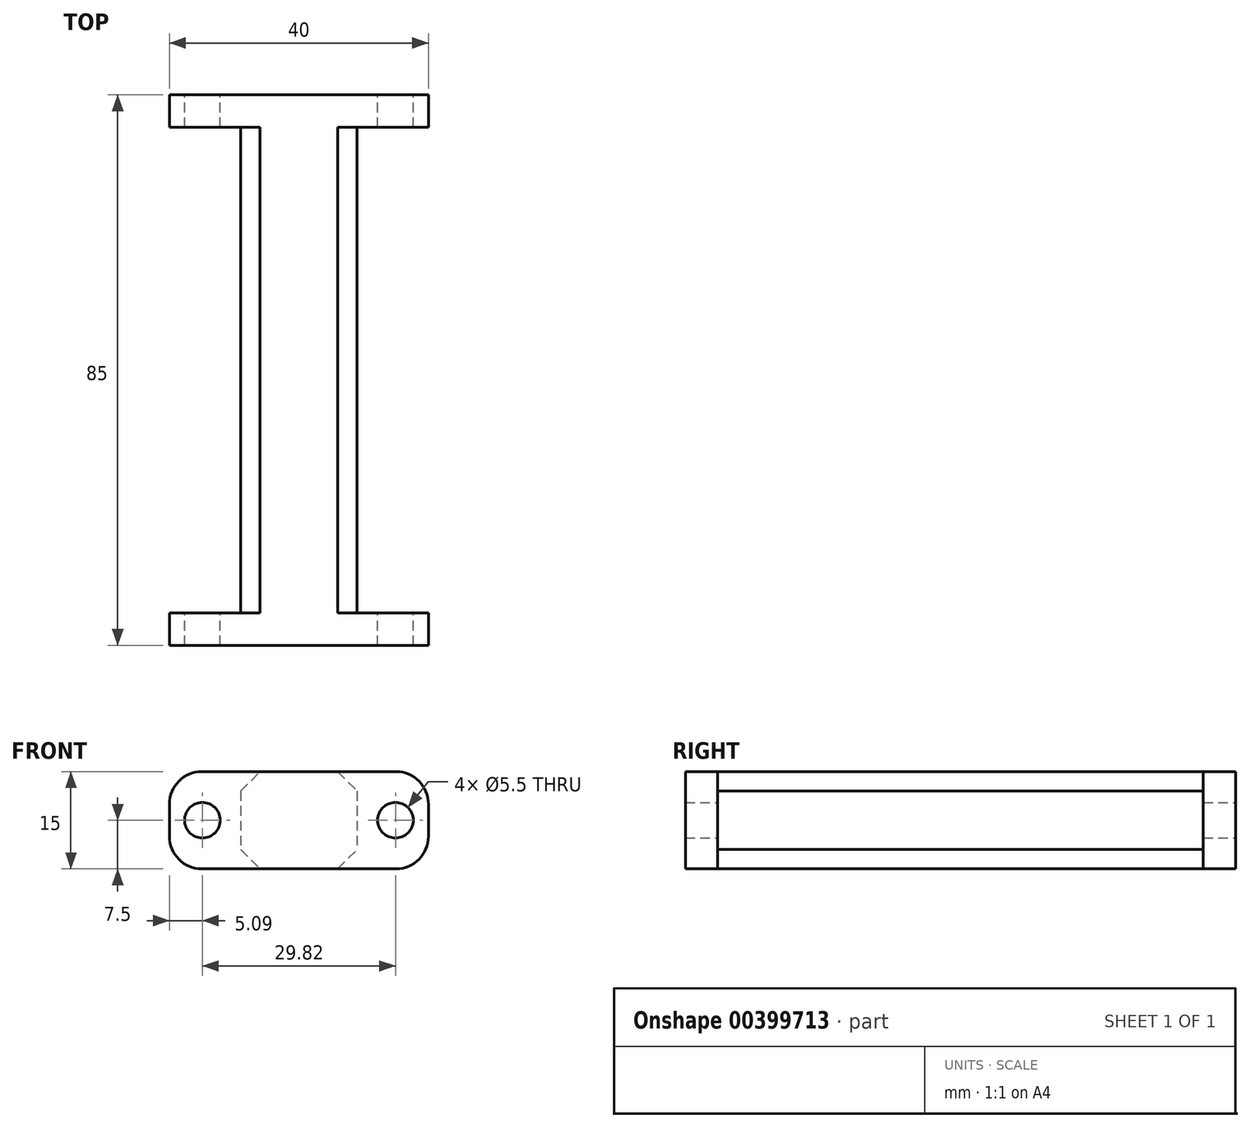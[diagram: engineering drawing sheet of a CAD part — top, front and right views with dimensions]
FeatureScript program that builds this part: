
annotation { "Feature Type Name" : "Feature", "Feature Type Description" : "" }
export const myFeature = defineFeature(function(context is Context, id is Id, definition is map)
    precondition{}
    {
        {
            var Q0;
            Q0=qCreatedBy(makeId("Top.planeOp"),FACE);
            var sketch = newSketch(context, id + "F0", { "sketchPlane" : qUnion([Q0])});
            skLineSegment(sketch, "E0.bottom", {"start": v(9, 37.5) * mm, "end": v(-9, 37.5) * mm});
            skLineSegment(sketch, "E0.top", {"start": v(9, -37.5) * mm, "end": v(-9, -37.5) * mm});
            skLineSegment(sketch, "E0.left", {"start": v(9, 37.5) * mm, "end": v(9, -37.5) * mm});
            skLineSegment(sketch, "E0.right", {"start": v(-9, 37.5) * mm, "end": v(-9, -37.5) * mm});
            skPoint(sketch, "E0.middle", {"position": v(0, 0) * mm});
            skLineSegment(sketch, "E1", {"start": v(0, -37.5) * mm, "end": v(0, -40) * mm});
            skPoint(sketch, "E1.endSnap0", {"position": v(0, -37.5) * mm});
            skLineSegment(sketch, "E2.bottom", {"start": v(20, -37.5) * mm, "end": v(-20, -37.5) * mm});
            skLineSegment(sketch, "E2.top", {"start": v(20, -42.5) * mm, "end": v(-20, -42.5) * mm});
            skLineSegment(sketch, "E2.left", {"start": v(20, -37.5) * mm, "end": v(20, -42.5) * mm});
            skLineSegment(sketch, "E2.right", {"start": v(-20, -37.5) * mm, "end": v(-20, -42.5) * mm});
            skPoint(sketch, "E2.middle", {"position": v(0, -40) * mm});
            skLineSegment(sketch, "E3", {"start": v(0, 37.5) * mm, "end": v(0, 40) * mm});
            skPoint(sketch, "E3.endSnap0", {"position": v(0, 37.5) * mm});
            skLineSegment(sketch, "E4.bottom", {"start": v(20, 42.5) * mm, "end": v(-20, 42.5) * mm});
            skLineSegment(sketch, "E4.top", {"start": v(20, 37.5) * mm, "end": v(-20, 37.5) * mm});
            skLineSegment(sketch, "E4.left", {"start": v(20, 42.5) * mm, "end": v(20, 37.5) * mm});
            skLineSegment(sketch, "E4.right", {"start": v(-20, 42.5) * mm, "end": v(-20, 37.5) * mm});
            skPoint(sketch, "E4.middle", {"position": v(0, 40) * mm});
            skSolve(sketch);
        }
        {
            var Q0;
            Q0=makeQuery(id+"F0.imprint","IMPRINT",FACE,{"disambiguationData":[TD([[makeQuery(id+"F0.imprint","IMPRINT",EDGE,{"derivedFrom":sQuery(id+"F0.wireOp",EDGE,"E4.bottom")}),1.0]])]});
            var Q1;
            {var subQ3=sQuery(id+"F0.wireOp",EDGE,"E0.left");Q1=makeQuery(id+"F0.imprint","IMPRINT",FACE,{"disambiguationData":[TD([[makeQuery(id+"F0.imprint","IMPRINT",EDGE,{"derivedFrom":subQ3}),-1.0]])]});}
            var Q2;
            Q2=makeQuery(id+"F0.imprint","IMPRINT",FACE,{"disambiguationData":[TD([[makeQuery(id+"F0.imprint","IMPRINT",EDGE,{"derivedFrom":sQuery(id+"F0.wireOp",EDGE,"E2.top")}),-1.0]])]});
            extrude(context, id + "F1", {"entities" : qUnion([Q0, Q1, Q2]), "depth" : 15 * mm});
        }
        {
            var Q0;
            Q0=makeQuery(id+"F1.opExtrude","CAP_EDGE",EDGE,{"disambiguationData":[OSD([sQuery(id+"F0.wireOp",EDGE,"E0.left")])],"isStart":true});
            var Q1;
            Q1=makeQuery(id+"F1.opExtrude","CAP_EDGE",EDGE,{"disambiguationData":[OSD([sQuery(id+"F0.wireOp",EDGE,"E0.right")])],"isStart":true});
            var Q2;
            Q2=makeQuery(id+"F1.opExtrude","CAP_EDGE",EDGE,{"disambiguationData":[OSD([sQuery(id+"F0.wireOp",EDGE,"E0.right")])],"isStart":false});
            var Q3;
            Q3=makeQuery(id+"F1.opExtrude","CAP_EDGE",EDGE,{"disambiguationData":[OSD([sQuery(id+"F0.wireOp",EDGE,"E0.left")])],"isStart":false});
            chamfer(context, id + "F2", {"entities" : qUnion([Q0, Q1, Q2, Q3]), "width" : 3 * mm, "tangentPropagation" : true});
        }
        {
            var Q0;
            Q0=makeQuery(id+"F1.opExtrude","CAP_EDGE",EDGE,{"disambiguationData":[OSD([sQuery(id+"F0.wireOp",EDGE,"E2.left")])],"isStart":false});
            var Q1;
            Q1=makeQuery(id+"F1.opExtrude","CAP_EDGE",EDGE,{"disambiguationData":[OSD([sQuery(id+"F0.wireOp",EDGE,"E2.right")])],"isStart":true});
            var Q2;
            Q2=makeQuery(id+"F1.opExtrude","CAP_EDGE",EDGE,{"disambiguationData":[OSD([sQuery(id+"F0.wireOp",EDGE,"E2.right")])],"isStart":false});
            var Q3;
            Q3=makeQuery(id+"F1.opExtrude","CAP_EDGE",EDGE,{"disambiguationData":[OSD([sQuery(id+"F0.wireOp",EDGE,"E2.left")])],"isStart":true});
            var Q4;
            Q4=makeQuery(id+"F1.opExtrude","CAP_EDGE",EDGE,{"disambiguationData":[OSD([sQuery(id+"F0.wireOp",EDGE,"E4.right")])],"isStart":false});
            var Q5;
            Q5=makeQuery(id+"F1.opExtrude","CAP_EDGE",EDGE,{"disambiguationData":[OSD([sQuery(id+"F0.wireOp",EDGE,"E4.right")])],"isStart":true});
            var Q6;
            Q6=makeQuery(id+"F1.opExtrude","CAP_EDGE",EDGE,{"disambiguationData":[OSD([sQuery(id+"F0.wireOp",EDGE,"E4.left")])],"isStart":true});
            var Q7;
            Q7=makeQuery(id+"F1.opExtrude","CAP_EDGE",EDGE,{"disambiguationData":[OSD([sQuery(id+"F0.wireOp",EDGE,"E4.left")])],"isStart":false});
            fillet(context, id + "F3", {"entities" : qUnion([Q0, Q1, Q2, Q3, Q4, Q5, Q6, Q7]), "radius" : 5 * mm, "tangentPropagation" : true, "allowEdgeOverflow" : false});
        }
        {
            var Q0;
            Q0=makeQuery(id+"F1.opExtrude","SWEPT_FACE",FACE,{"disambiguationData":[OSD([sQuery(id+"F0.wireOp",EDGE,"E4.bottom")])]});
            var sketch = newSketch(context, id + "F4", { "sketchPlane" : qUnion([Q0])});
            skLineSegment(sketch, "E5", {"start": v(0, 0) * mm, "end": v(0, 7.5) * mm});
            skPoint(sketch, "E5.endSnap0", {"position": v(0, 0) * mm});
            skLineSegment(sketch, "E6", {"start": v(0, 7.5) * mm, "end": v(14.9, 7.5) * mm});
            skLineSegment(sketch, "E7", {"start": v(0, 7.5) * mm, "end": v(-14.9, 7.5) * mm});
            skCircle(sketch, "E8", {"center": v(-14.9, 7.5) * mm, "radius": 2.75 * mm});
            skCircle(sketch, "E9", {"center": v(14.9, 7.5) * mm, "radius": 2.75 * mm});
            skSolve(sketch);
        }
        {
            var Q0;
            Q0 = qSketchRegion(id + "F4", true);
            extrude(context, id + "F5", {"entities" : qUnion([Q0]), "operationType" : NewBodyOperationType.REMOVE, "oppositeDirection" : true, "depth" : 150 * mm});
        }
    });
